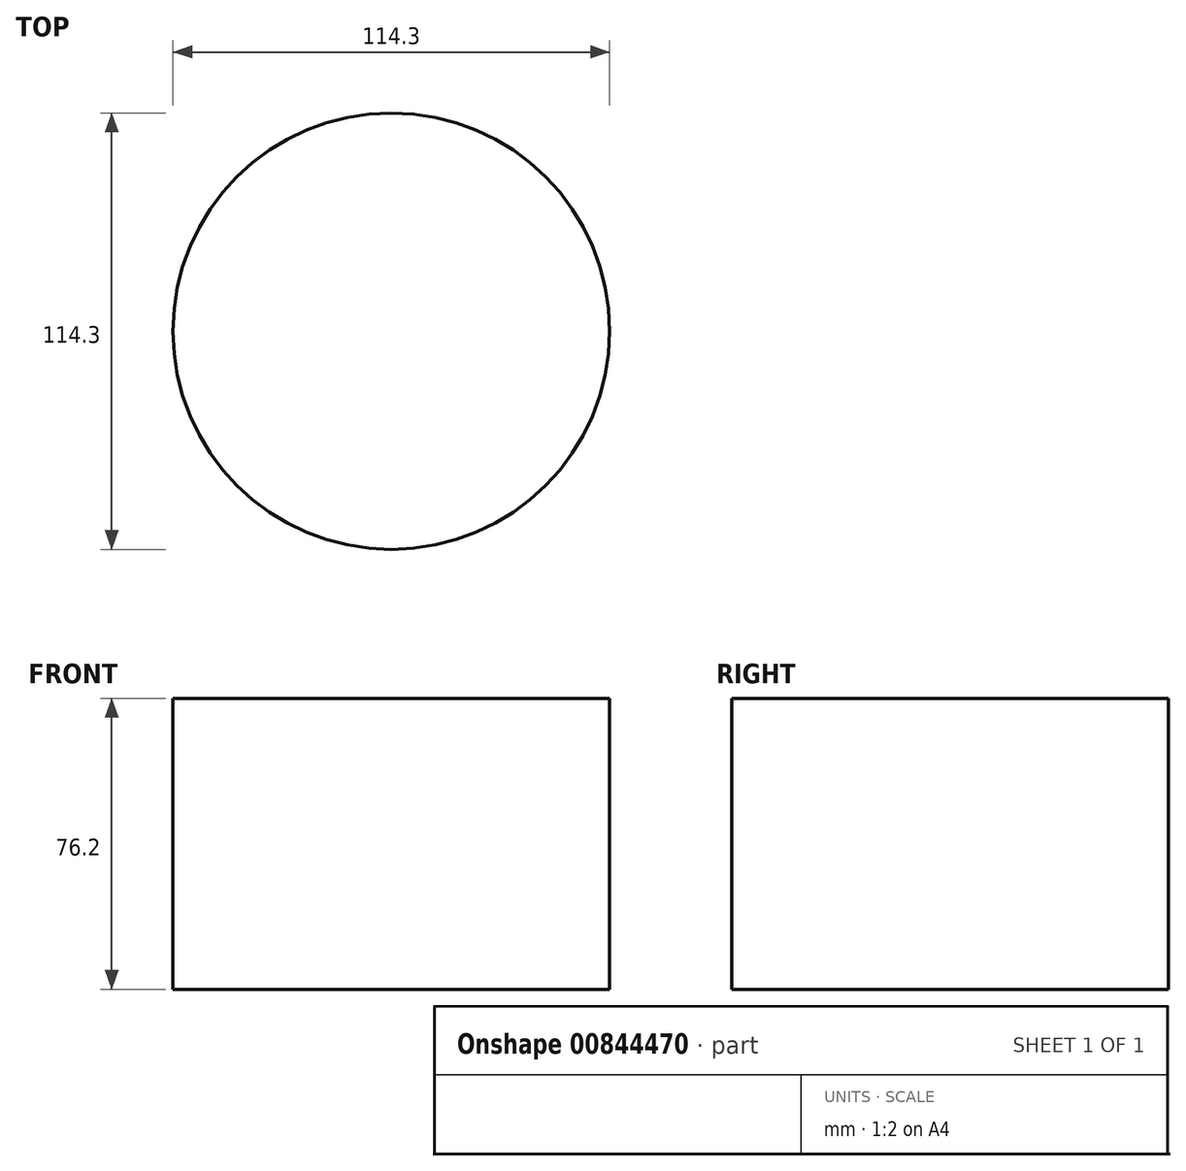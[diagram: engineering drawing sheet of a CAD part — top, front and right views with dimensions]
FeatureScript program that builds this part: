
annotation { "Feature Type Name" : "Feature", "Feature Type Description" : "" }
export const myFeature = defineFeature(function(context is Context, id is Id, definition is map)
    precondition{}
    {
        {
            var Q0;
            Q0=qCreatedBy(makeId("Top.planeOp"),FACE);
            var sketch = newSketch(context, id + "F0", { "sketchPlane" : qUnion([Q0])});
            skCircle(sketch, "E0", {"center": v(0, 0) * mm, "radius": 57.15 * mm});
            skSolve(sketch);
        }
        {
            var Q0;
            Q0=makeQuery(id+"F0.imprint","IMPRINT",FACE,{"disambiguationData":[TD([[makeQuery(id+"F0.imprint","IMPRINT",EDGE,{"derivedFrom":sQuery(id+"F0.wireOp",EDGE,"E0")}),1.0]])]});
            extrude(context, id + "F1", {"entities" : qUnion([Q0]), "depth" : 76.2 * mm, "offsetDistance" : 25.4 * mm});
        }
    });
